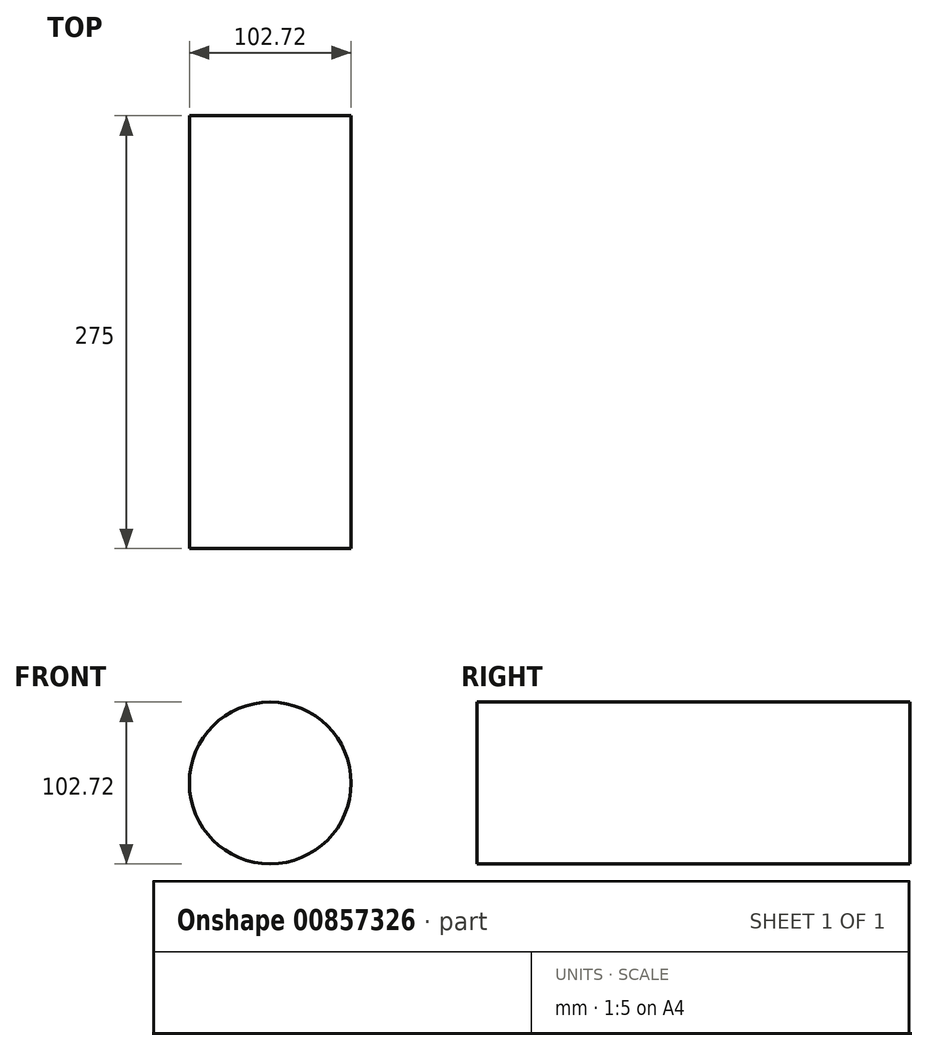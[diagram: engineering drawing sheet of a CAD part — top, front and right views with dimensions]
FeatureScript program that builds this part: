
annotation { "Feature Type Name" : "Feature", "Feature Type Description" : "" }
export const myFeature = defineFeature(function(context is Context, id is Id, definition is map)
    precondition{}
    {
        {
            var Q0;
            Q0=qCreatedBy(makeId("Front.planeOp"),FACE);
            var sketch = newSketch(context, id + "F0", { "sketchPlane" : qUnion([Q0])});
            skCircle(sketch, "E0", {"center": v(0, 0) * mm, "radius": 51.36 * mm});
            skSolve(sketch);
        }
        {
            var Q0;
            Q0=makeQuery(id+"F0.imprint","IMPRINT",FACE,{"disambiguationData":[TD([[makeQuery(id+"F0.imprint","IMPRINT",EDGE,{"derivedFrom":sQuery(id+"F0.wireOp",EDGE,"E0")}),1.0]])]});
            var Q1;
            Q1=sQuery(id+"F0.wireOp",EDGE,"E0");
            extrude(context, id + "F1", {"entities" : qUnion([Q0]), "surfaceEntities" : qUnion([Q1]), "depth" : 275 * mm, "offsetDistance" : 25.4 * mm});
        }
    });
